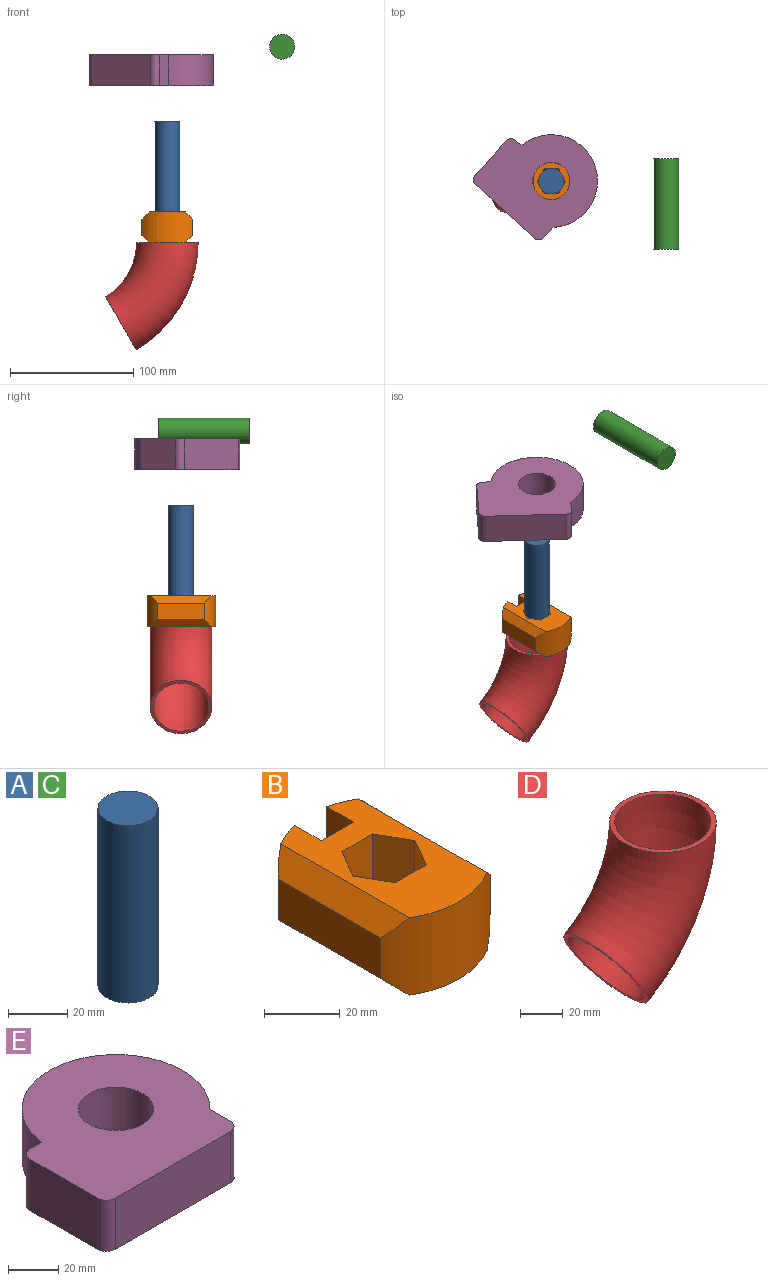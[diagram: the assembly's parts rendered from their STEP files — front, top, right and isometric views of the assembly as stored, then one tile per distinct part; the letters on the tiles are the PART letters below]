
ASSEMBLY  parts=5 mates=4
PART A: 3 faces, bbox 20.3x20.3x73.3 mm
  f0: cylinder r=10.14mm len=73.3mm, axis (0,0,-1), area 4670.1mm2, adj f1,f2
  f1: plane 20.28x20.28mm, normal (0,0,1), area 323mm2, adj f0
  f2: plane 20.28x20.28mm, normal (0,0,-1), area 323mm2, adj f0
PART B: 20 faces, bbox 41.1x55.3x25 mm
  f0: cylinder r=28mm len=25mm, axis (0,0,-1), area 376.6mm2, adj f3,f4,f5,f15,f18,f19
  f1: cylinder r=28mm len=41.06mm, axis (0,0,-1), area 1055.5mm2, adj f3,f4,f14,f15,f16,f17,f18,f19
  f2: cylinder r=28mm len=25mm, axis (0,0,-1), area 376.6mm2, adj f3,f4,f6,f14,f16,f17
  f3: plane 55.35x29.06mm, normal (0,0,1), area 1080.7mm2, adj f0,f1,f2,f5,f6,f7,f8,f9
  f4: plane 55.35x29.06mm, normal (0,0,-1), area 1080.7mm2, adj f0,f1,f2,f5,f6,f7,f8,f9
  f5: plane 25x9.9mm, normal (1,0,0), area 247.4mm2, adj f0,f3,f4,f7
  f6: plane 25x9.9mm, normal (-1,0,0), area 247.4mm2, adj f2,f3,f4,f7
  f7: plane 25x12mm, normal (0,1,0), area 300mm2, adj f3,f4,f5,f6
  f8: plane 25x10mm, normal (-0.87,0.5,0), area 288.7mm2, adj f3,f4,f9,f13
  f9: plane 25x10mm, normal (-0.87,-0.5,0), area 288.7mm2, adj f3,f4,f8,f10
  f10: plane 25x11.55mm, normal (0,-1,0), area 288.7mm2, adj f3,f4,f9,f11
  f11: plane 25x10mm, normal (0.87,-0.5,0), area 288.7mm2, adj f3,f4,f10,f12
  f12: plane 25x10mm, normal (0.87,0.5,0), area 288.7mm2, adj f3,f4,f11,f13
  f13: plane 25x11.55mm, normal (0,1,0), area 288.7mm2, adj f3,f4,f8,f12
  f14: plane 38.08x13mm, normal (1,0,0), area 495mm2, adj f1,f2,f16,f17
  f15: plane 38.08x13mm, normal (-1,0,0), area 495mm2, adj f0,f1,f18,f19
  f16: plane 47.87x6mm, normal (0.71,0,0.71), area 368.6mm2, adj f1,f2,f3,f14
  f17: plane 47.87x6mm, normal (0.71,0,-0.71), area 368.6mm2, adj f1,f2,f4,f14
  f18: plane 47.87x6mm, normal (-0.71,0,0.71), area 368.6mm2, adj f0,f1,f3,f15
  f19: plane 47.87x6mm, normal (-0.71,0,-0.71), area 368.6mm2, adj f0,f1,f4,f15
PART C: same geometry as A
PART D: 4 faces, bbox 83.4x50x94 mm
  f0: torus R=75.27mm, axis (0,-1,0), area 12382.2mm2, adj f1,f2
  f1: plane 50x43.3mm, normal (-0.87,0,-0.5), area 373.1mm2, adj f0,f3
  f2: plane 50x50mm, normal (0,0,1), area 373.1mm2, adj f0,f3
  f3: torus R=75.27mm, axis (0,-1,0), area 11144mm2, adj f1,f2
PART E: 11 faces, bbox 86.3x80.8x25 mm
  f0: cylinder r=37.5mm len=74.7mm, axis (0,0,-1), area 3575.7mm2, adj f1,f4,f5,f6
  f1: plane 25x6.62mm, normal (0,1,0), area 165.4mm2, adj f0,f5,f6,f7
  f2: plane 38x25mm, normal (-1,0,0), area 950mm2, adj f5,f6,f7,f8
  f3: plane 65x25mm, normal (0,-1,0), area 1625mm2, adj f5,f6,f8,f9
  f4: plane 25x11.45mm, normal (1,0,0), area 286.3mm2, adj f0,f5,f6,f9
  f5: plane 86.32x80.8mm, normal (0,0,1), area 4997.1mm2, adj f0,f1,f2,f3,f4,f7,f8,f9
  f6: plane 86.32x80.8mm, normal (0,0,-1), area 4997.1mm2, adj f0,f1,f2,f3,f4,f7,f8,f9
  f7: cylinder r=5mm len=25mm, axis (0,0,1), area 196.3mm2, adj f1,f2,f5,f6
  f8: cylinder r=5mm len=25mm, axis (0,0,-1), area 196.3mm2, adj f2,f3,f5,f6
  f9: cylinder r=5mm len=25mm, axis (0,0,1), area 196.3mm2, adj f3,f4,f5,f6
  f10: cylinder r=15mm len=30mm, axis (0,0,1), area 2356.2mm2, adj f5,f6
PLACE A t=(0.05,0.19,12.26)mm
PLACE B t=(0.05,0.19,-0.24)mm fixed
PLACE C rot(axis=(-1,0,0),90deg) t=(93.12,-55.09,145.92)mm
PLACE D t=(0.05,0.19,-12.74)mm
PLACE E rot(axis=(0,0,-1),42.3deg) t=(-22.28,-6.53,114.44)mm
MATE planar D.f2 <-> B.f4  axis (0,0,1) through (0.05,0.19,-12.74)mm
MATE cylindrical A.f0 <-> B.f0  axis (0,0,-1) through (0.05,0.19,12.26)mm
MATE cylindrical E.f0 <-> A.f0  axis (0,0,1) through (0.05,0.19,139.44)mm
MATE cylindrical D.f2 <-> A.f0  axis (0,0,1) through (0.05,0.19,-12.74)mm
